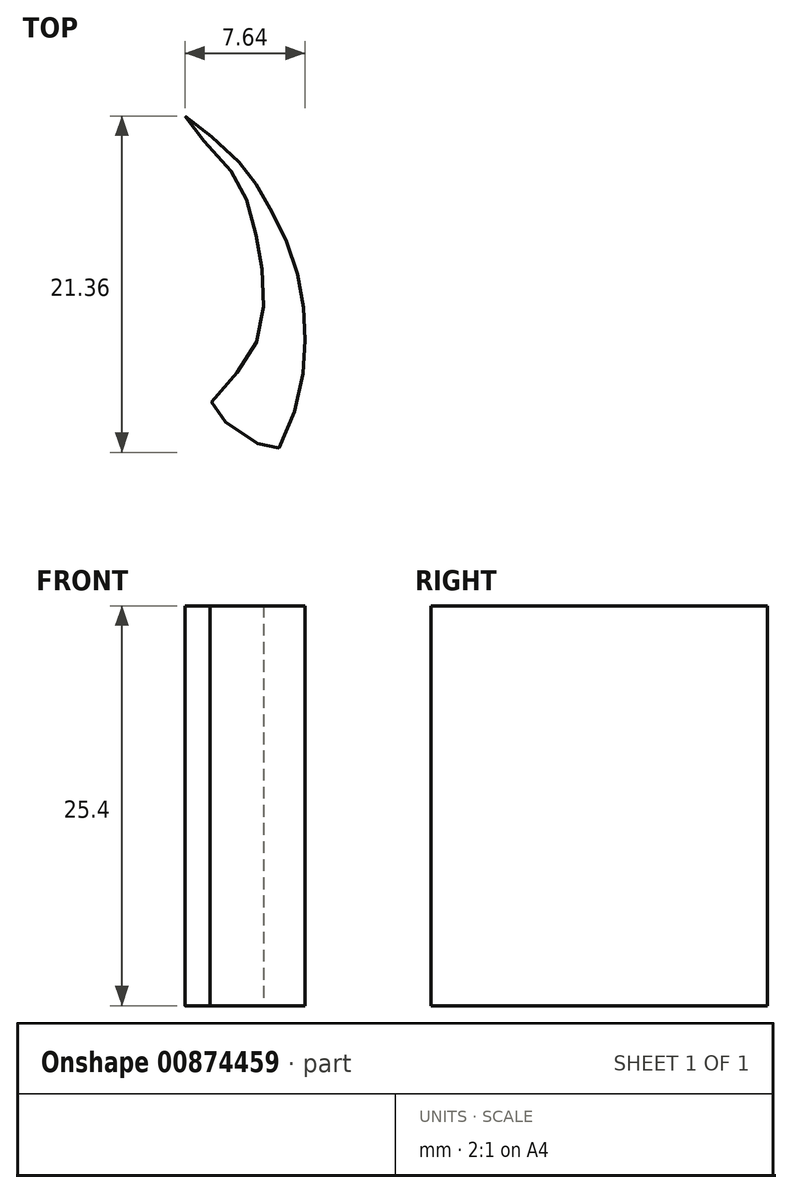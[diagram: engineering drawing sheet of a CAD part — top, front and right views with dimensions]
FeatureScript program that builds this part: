
annotation { "Feature Type Name" : "Feature", "Feature Type Description" : "" }
export const myFeature = defineFeature(function(context is Context, id is Id, definition is map)
    precondition{}
    {
        {
            var Q0;
            Q0=qCreatedBy(makeId("Top.planeOp"),FACE);
            var sketch = newSketch(context, id + "F0", { "sketchPlane" : qUnion([Q0])});
            skFitSpline(sketch, "E0", {"points": [v(6.83, 35.5) * mm, v(8.91, 34.42) * mm, v(10.83, 33.34) * mm, v(13.59, 30.75) * mm, v(16.34, 27.25) * mm, v(17.93, 23.74) * mm, v(18.93, 17.57) * mm, v(18.26, 12.98) * mm, v(17.34, 10.06) * mm, v(20.51, 9.14) * mm, v(24.18, 7.72) * mm, v(28.1, 5.22) * mm, v(31.6, 0.71) * mm, v(33.86, -4.54) * mm, v(34.43, -7.5) * mm, v(34.2, -11.56) * mm, v(33.64, -11.75) * mm, v(33.07, -11.25) * mm, v(32.95, -14.02) * mm, v(32.44, -16.04) * mm, v(31.43, -18.38) * mm, v(29.1, -21.16) * mm, v(27.51, -22.42) * mm, v(26.44, -22.93) * mm, v(27.2, -23.56) * mm, v(25.56, -24.82) * mm, v(23.22, -26.15) * mm, v(20.25, -27.28) * mm, v(18.04, -27.73) * mm, v(15.33, -27.79) * mm, v(12.74, -27.73) * mm, v(10.28, -27.03) * mm, v(7.3, -25.83) * mm, v(4.4, -24.25) * mm, v(2.07, -22.36) * mm, v(0, -20.4) * mm, v(-0.9, -21.41) * mm, v(-3.17, -23.5) * mm, v(-6.08, -25.39) * mm, v(-9.55, -27.22) * mm, v(-16.42, -27.97) * mm, v(-19.11, -27.78) * mm, v(-21.14, -27.08) * mm, v(-24.13, -26.05) * mm, v(-25.79, -25.13) * mm, v(-27.25, -24.07) * mm, v(-26.57, -23.32) * mm, v(-28.08, -22.34) * mm, v(-29.06, -21.62) * mm, v(-30.28, -20.25) * mm, v(-31.47, -18.6) * mm, v(-32.74, -15.85) * mm, v(-33.2, -12.9) * mm, v(-33.33, -11.84) * mm, v(-34.07, -12.32) * mm, v(-34.5, -11.88) * mm, v(-34.6, -9.17) * mm, v(-34.46, -6.73) * mm, v(-33.67, -4.02) * mm, v(-32.78, -1.17) * mm, v(-31.5, 1.08) * mm, v(-29.68, 3.38) * mm, v(-27, 5.84) * mm, v(-24.09, 7.6) * mm, v(-21.29, 8.7) * mm, v(-18.82, 9.42) * mm, v(-17.51, 9.81) * mm, v(-18.43, 12.03) * mm, v(-19.27, 16.45) * mm, v(-19.08, 19.29) * mm, v(-18.72, 22.24) * mm, v(-17.57, 25.11) * mm, v(-15.93, 28.43) * mm, v(-13.66, 31.12) * mm, v(-10.38, 33.65) * mm, v(-7.51, 35.25) * mm, v(-6.84, 34.57) * mm, v(-4.99, 35.58) * mm, v(-2.46, 36.34) * mm, v(0, 36.68) * mm, v(2.5, 36.09) * mm, v(5.03, 35.41) * mm, v(6.2, 34.9) * mm, v(6.83, 35.5) * mm]});
            skFitSpline(sketch, "E1", {"points": [v(-7.6, 34.15) * mm, v(-9.7, 32.38) * mm, v(-11.64, 29.7) * mm, v(-13.07, 26.83) * mm, v(-13.91, 23.63) * mm, v(-13.91, 19.76) * mm, v(-13.4, 16.81) * mm, v(-12.14, 13.53) * mm, v(-9.87, 14.88) * mm, v(-8.19, 15.89) * mm, v(-9.03, 17.07) * mm, v(-10.38, 19.26) * mm, v(-11.39, 21.78) * mm, v(-11.72, 24.9) * mm, v(-11.47, 27.59) * mm], "startDerivative": vector(-30.82, -22.79) * mm, "endDerivative": vector(5.06, 37.48) * mm});
            skPoint(sketch, "E2.first.point", {"position": v(0, 0) * mm});
            skPoint(sketch, "E2.third.point", {"position": v(7.3, 3.25) * mm});
            skFitSpline(sketch, "E3", {"points": [v(7.81, 16.27) * mm, v(9.99, 14.82) * mm, v(11.8, 13.56) * mm, v(13.16, 16.1) * mm, v(13.8, 19.45) * mm, v(13.8, 21.98) * mm, v(13.43, 24.6) * mm, v(12.52, 27.24) * mm, v(11.35, 29.5) * mm, v(10.17, 31.4) * mm, v(8.63, 32.94) * mm, v(6.2, 34.9) * mm, v(8.08, 32.58) * mm, v(9.8, 30.4) * mm, v(10.71, 27.42) * mm, v(11.16, 24.6) * mm, v(10.98, 21.26) * mm, v(9.53, 18.63) * mm, v(7.81, 16.27) * mm]});
            skFitSpline(sketch, "E4", {"points": [v(-11.47, 27.59) * mm, v(-10.57, 29.75) * mm, v(-9.7, 31.48) * mm, v(-8.27, 33.1) * mm, v(-7.6, 34.15) * mm], "startDerivative": vector(3.36, 8.02) * mm, "endDerivative": vector(2.71, 5.03) * mm});
            skFitSpline(sketch, "E5", {"points": [v(-7.6, 8.6) * mm, v(-6.46, 9.46) * mm, v(-5.1, 10.27) * mm, v(-3.4, 10.86) * mm, v(-1.72, 11.22) * mm, v(0, 11.3) * mm, v(1.75, 11.08) * mm, v(3.46, 10.5) * mm, v(5.13, 10.1) * mm, v(6.85, 9.14) * mm, v(7.43, 8.83) * mm, v(9.46, 10.18) * mm, v(8.56, 11.26) * mm, v(7.16, 12.12) * mm, v(6.2, 12.84) * mm, v(4.55, 13.34) * mm, v(3.28, 13.43) * mm, v(1.34, 13.11) * mm, v(-1.32, 13.02) * mm, v(-3.98, 13.47) * mm, v(-6, 12.84) * mm, v(-8.8, 11.13) * mm, v(-9.7, 10.36) * mm, v(-7.6, 8.6) * mm]});
            skFitSpline(sketch, "E6", {"points": [v(11.26, 1.97) * mm, v(11.45, -1.07) * mm, v(11.07, -3.35) * mm, v(9.86, -6.2) * mm, v(8.03, -8.41) * mm, v(5.43, -10.25) * mm, v(3.91, -11.07) * mm, v(4.16, -13.48) * mm, v(6.76, -12.6) * mm, v(8.85, -11.14) * mm, v(9.74, -10.38) * mm, v(10.5, -7.78) * mm, v(11.83, -5.5) * mm, v(13.47, -3.6) * mm, v(13.85, -2.14) * mm, v(13.98, 0) * mm, v(13.79, 1.47) * mm, v(13.6, 3.05) * mm, v(11.26, 1.97) * mm]});
            skFitSpline(sketch, "E7", {"points": [v(17.45, 3.05) * mm, v(17.88, 0.54) * mm, v(17.88, -1.17) * mm, v(19.1, -1.17) * mm, v(21.36, -0.87) * mm, v(24.6, -1.48) * mm, v(27.54, -2.52) * mm, v(29.74, -4.35) * mm, v(31.33, -6.55) * mm, v(32.86, -9.86) * mm, v(32.37, -7.29) * mm, v(31.52, -5.15) * mm, v(30.3, -3.31) * mm, v(28.95, -1.3) * mm, v(26.8, 0.54) * mm, v(24.48, 2.07) * mm, v(22.28, 3.05) * mm, v(19.83, 3.6) * mm, v(18.18, 3.78) * mm, v(17.45, 3.05) * mm]});
            skFitSpline(sketch, "E8", {"points": [v(9.93, -14.93) * mm, v(7.08, -16.54) * mm, v(6.2, -17.16) * mm, v(5.6, -17.29) * mm, v(7.08, -19.27) * mm, v(9.87, -21.63) * mm, v(12.6, -23.5) * mm, v(14.7, -24.17) * mm, v(17.18, -24.72) * mm, v(19.66, -24.72) * mm, v(21.83, -24.54) * mm, v(23.69, -24.04) * mm, v(24.8, -23.5) * mm, v(22.26, -24.1) * mm, v(18.73, -23.5) * mm, v(16.06, -22.74) * mm, v(13.98, -21.13) * mm, v(12.04, -19.15) * mm, v(10.98, -17.29) * mm, v(10.49, -15.92) * mm, v(9.93, -14.93) * mm]});
            skFitSpline(sketch, "E9", {"points": [v(-9.7, -15.27) * mm, v(-8.32, -16.2) * mm, v(-6.08, -17.29) * mm, v(-7.6, -19.24) * mm, v(-9.7, -21.5) * mm, v(-12.34, -23.32) * mm, v(-15.1, -24.34) * mm, v(-16.67, -24.77) * mm, v(-19.43, -25.39) * mm, v(-22.34, -24.77) * mm, v(-24.82, -24.13) * mm, v(-21.06, -24.13) * mm, v(-17.66, -23.5) * mm, v(-14.9, -22.22) * mm, v(-12.9, -20.45) * mm, v(-11.47, -18.1) * mm, v(-10.36, -15.77) * mm, v(-9.7, -15.27) * mm]});
            skFitSpline(sketch, "E10", {"points": [v(-11.5, 2.13) * mm, v(-11.57, -0.86) * mm, v(-11.03, -3.55) * mm, v(-10.19, -5.7) * mm, v(-8.42, -8.15) * mm, v(-6.04, -10) * mm, v(-3.9, -11.15) * mm, v(-4.13, -13.53) * mm, v(-5.81, -13.45) * mm, v(-7.2, -12.68) * mm, v(-8.8, -11.6) * mm, v(-9.88, -10.46) * mm, v(-10.72, -8.61) * mm, v(-12.1, -6.24) * mm, v(-13.26, -4.7) * mm, v(-14.18, -3.17) * mm, v(-14.56, -1.02) * mm, v(-14.56, 0.98) * mm, v(-14.02, 2.82) * mm, v(-11.5, 2.13) * mm]});
            skFitSpline(sketch, "E11", {"points": [v(-17.72, 3.39) * mm, v(-17.99, 0.76) * mm, v(-17.99, -1.4) * mm, v(-20.09, -1.08) * mm, v(-22.45, -1.08) * mm, v(-25.4, -1.86) * mm, v(-27.9, -3.11) * mm, v(-30.26, -4.7) * mm, v(-31.84, -7.12) * mm, v(-32.76, -9.35) * mm, v(-32.76, -8.03) * mm, v(-32.3, -6.66) * mm, v(-31.38, -4.7) * mm, v(-30.26, -3.11) * mm, v(-28.82, -1.67) * mm, v(-27.18, 0) * mm, v(-25.08, 1.35) * mm, v(-22.98, 2.34) * mm, v(-20.88, 3.13) * mm, v(-19.04, 3.39) * mm, v(-17.72, 3.39) * mm]});
            skSolve(sketch);
        }
        {
            var Q0;
            {var subQ0=sQuery(id+"F0.wireOp",EDGE,"E0");Q0=makeQuery(id+"F0.imprint","IMPRINT",FACE,{"disambiguationData":[TD([[makeQuery(id+"F0.imprint","IMPRINT",EDGE,{"derivedFrom":subQ0}),-1.0]])]});}
            extrude(context, id + "F1", {"entities" : qUnion([Q0]), "depth" : 25.4 * mm, "offsetDistance" : 25.4 * mm});
        }
    });
